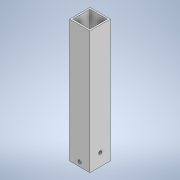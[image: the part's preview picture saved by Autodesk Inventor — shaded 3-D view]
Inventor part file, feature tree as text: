
AUTODESK INVENTOR PART (.ipt)
format: ipt  version: 2022 (Build 260153000, 153)  size: 116,736 bytes
history: native  units: mm
features: extrude x3, sketch x3
ambient origin geometry x8: Origin, YZ Plane, XZ Plane, XY Plane, X Axis, Y Axis, Z Axis, Center Point
bodies: Solid1 (feature_tree)
feature tree (6):
  extrude  "Extrusion1"  Depth=25.4mm
  extrude  "Extrusion2"  Depth=152.4mm TaperAngle=0.0deg
  extrude  "Extrusion3"  Depth=152.4mm TaperAngle=0.0deg
  sketch  "Sketch1"  dims[d0=25.4mm d1=25.4mm]
  sketch  "Sketch2"  dims[d2=2.0mm d3=152.4mm d4=0.0mm]
  sketch  "Sketch3"  dims[d6=4.0mm d7=152.4mm d8=0.0mm d10=4.0mm d11=0.0mm d12=0.0mm]
